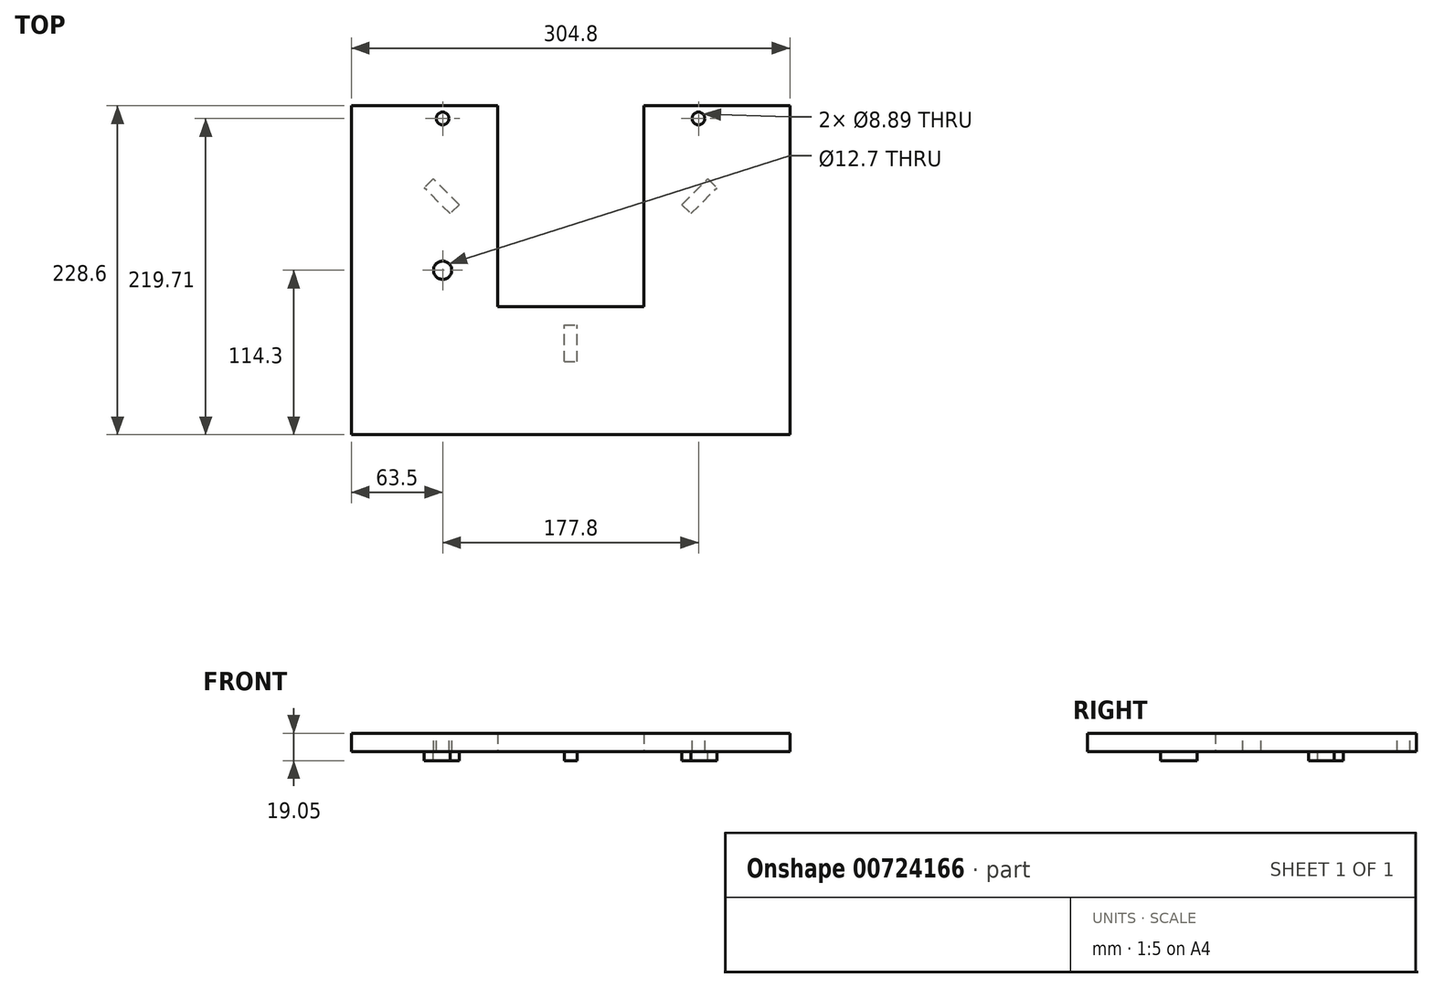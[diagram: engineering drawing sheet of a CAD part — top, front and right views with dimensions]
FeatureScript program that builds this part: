
annotation { "Feature Type Name" : "Feature", "Feature Type Description" : "" }
export const myFeature = defineFeature(function(context is Context, id is Id, definition is map)
    precondition{}
    {
        {
            var Q0;
            Q0=qCreatedBy(makeId("Top.planeOp"),FACE);
            var sketch = newSketch(context, id + "F0", { "sketchPlane" : qUnion([Q0])});
            skLineSegment(sketch, "E0.bottom", {"start": v(152.4, 114.3) * mm, "end": v(-152.4, 114.3) * mm});
            skLineSegment(sketch, "E0.top", {"start": v(152.4, -114.3) * mm, "end": v(-152.4, -114.3) * mm});
            skLineSegment(sketch, "E0.left", {"start": v(152.4, 114.3) * mm, "end": v(152.4, -114.3) * mm});
            skLineSegment(sketch, "E0.right", {"start": v(-152.4, 114.3) * mm, "end": v(-152.4, -114.3) * mm});
            skPoint(sketch, "E0.middle", {"position": v(0, 0) * mm});
            skLineSegment(sketch, "E1.bottom", {"start": v(-50.8, 114.3) * mm, "end": v(50.8, 114.3) * mm});
            skLineSegment(sketch, "E1.top", {"start": v(-50.8, -25.4) * mm, "end": v(50.8, -25.4) * mm});
            skLineSegment(sketch, "E1.left", {"start": v(-50.8, 114.3) * mm, "end": v(-50.8, -25.4) * mm});
            skLineSegment(sketch, "E1.right", {"start": v(50.8, 114.3) * mm, "end": v(50.8, -25.4) * mm});
            skLineSegment(sketch, "E2", {"start": v(50.8, 67.36) * mm, "end": v(152.4, 67.36) * mm, "construction": true});
            skSolve(sketch);
        }
        {
            var Q0;
            Q0=makeQuery(id+"F0.imprint","IMPRINT",FACE,{"disambiguationData":[TD([[makeQuery(id+"F0.imprint","IMPRINT",EDGE,{"derivedFrom":sQuery(id+"F0.wireOp",EDGE,"E0.bottom")}),1.0]])]});
            extrude(context, id + "F1", {"entities" : qUnion([Q0]), "depth" : 12.7 * mm, "offsetDistance" : 25.4 * mm});
        }
        {
            var Q0;
            Q0=makeQuery(id+"F1.opExtrude","CAP_FACE",FACE,{"disambiguationData":[OSD([sQuery(id+"F0.wireOp",EDGE,"E0.bottom"),sQuery(id+"F0.wireOp",EDGE,"E0.top"),sQuery(id+"F0.wireOp",EDGE,"E0.left"),sQuery(id+"F0.wireOp",EDGE,"E0.right"),sQuery(id+"F0.wireOp",EDGE,"E1.top"),sQuery(id+"F0.wireOp",EDGE,"E1.left"),sQuery(id+"F0.wireOp",EDGE,"E1.right")])],"isStart":false});
            var sketch = newSketch(context, id + "F2", { "sketchPlane" : qUnion([Q0])});
            skLineSegment(sketch, "E3", {"start": v(0, 0) * mm, "end": v(0, 105.41) * mm, "construction": true});
            skLineSegment(sketch, "E4", {"start": v(0, 105.41) * mm, "end": v(-88.9, 105.41) * mm, "construction": true});
            skLineSegment(sketch, "E5", {"start": v(0, 105.41) * mm, "end": v(88.9, 105.41) * mm, "construction": true});
            skCircle(sketch, "E6", {"center": v(-88.9, 105.41) * mm, "radius": 4.45 * mm});
            skCircle(sketch, "E7", {"center": v(88.9, 105.41) * mm, "radius": 4.45 * mm});
            skSolve(sketch);
        }
        {
            var Q0;
            Q0=makeQuery(id+"F1.opExtrude","CAP_FACE",FACE,{"disambiguationData":[OSD([sQuery(id+"F0.wireOp",EDGE,"E0.bottom"),sQuery(id+"F0.wireOp",EDGE,"E0.top"),sQuery(id+"F0.wireOp",EDGE,"E0.left"),sQuery(id+"F0.wireOp",EDGE,"E0.right"),sQuery(id+"F0.wireOp",EDGE,"E1.top"),sQuery(id+"F0.wireOp",EDGE,"E1.left"),sQuery(id+"F0.wireOp",EDGE,"E1.right")])],"isStart":false});
            var sketch = newSketch(context, id + "F3", { "sketchPlane" : qUnion([Q0])});
            skLineSegment(sketch, "E8", {"start": v(0, 0) * mm, "end": v(-88.9, 0) * mm, "construction": true});
            skCircle(sketch, "E9", {"center": v(-88.9, 0) * mm, "radius": 6.35 * mm});
            skSolve(sketch);
        }
        {
            var Q0;
            Q0 = qSketchRegion(id + "F3", true);
            extrude(context, id + "F4", {"entities" : qUnion([Q0]), "operationType" : NewBodyOperationType.REMOVE, "oppositeDirection" : true, "depth" : 25.4 * mm, "offsetDistance" : 25.4 * mm});
        }
        {
            var Q0;
            Q0 = qSketchRegion(id + "F2", true);
            extrude(context, id + "F5", {"entities" : qUnion([Q0]), "operationType" : NewBodyOperationType.REMOVE, "oppositeDirection" : true, "depth" : 25.4 * mm, "offsetDistance" : 25.4 * mm});
        }
        {
            var Q0;
            Q0=makeQuery(id+"F1.opExtrude","CAP_FACE",FACE,{"disambiguationData":[OSD([sQuery(id+"F0.wireOp",EDGE,"E0.bottom"),sQuery(id+"F0.wireOp",EDGE,"E0.top"),sQuery(id+"F0.wireOp",EDGE,"E0.left"),sQuery(id+"F0.wireOp",EDGE,"E0.right"),sQuery(id+"F0.wireOp",EDGE,"E1.top"),sQuery(id+"F0.wireOp",EDGE,"E1.left"),sQuery(id+"F0.wireOp",EDGE,"E1.right")])],"isStart":true});
            var sketch = newSketch(context, id + "F6", { "sketchPlane" : qUnion([Q0])});
            skLineSegment(sketch, "E10", {"start": v(0, 0) * mm, "end": v(0, 143.7) * mm, "construction": true});
            skPoint(sketch, "E11.middle", {"position": v(0, 0) * mm});
            skLineSegment(sketch, "E12.bottom", {"start": v(77.41, -45.6) * mm, "end": v(83.7, -39.31) * mm});
            skLineSegment(sketch, "E12.top", {"start": v(95.38, -63.56) * mm, "end": v(101.66, -57.28) * mm});
            skLineSegment(sketch, "E12.left", {"start": v(77.41, -45.6) * mm, "end": v(95.38, -63.56) * mm});
            skLineSegment(sketch, "E12.right", {"start": v(83.7, -39.31) * mm, "end": v(101.66, -57.28) * mm});
            skLineSegment(sketch, "E13.bottom", {"start": v(-4.45, 63.5) * mm, "end": v(4.44, 63.5) * mm});
            skLineSegment(sketch, "E13.top", {"start": v(-4.45, 38.1) * mm, "end": v(4.44, 38.1) * mm});
            skLineSegment(sketch, "E13.left", {"start": v(-4.45, 63.5) * mm, "end": v(-4.45, 38.1) * mm});
            skLineSegment(sketch, "E13.right", {"start": v(4.45, 63.5) * mm, "end": v(4.45, 38.1) * mm});
            skPoint(sketch, "E13.middle", {"position": v(0, 50.8) * mm});
            skLineSegment(sketch, "E14.bottom", {"start": v(-77.41, -45.6) * mm, "end": v(-83.7, -39.31) * mm});
            skLineSegment(sketch, "E14.top", {"start": v(-95.38, -63.56) * mm, "end": v(-101.66, -57.28) * mm});
            skLineSegment(sketch, "E14.left", {"start": v(-77.41, -45.6) * mm, "end": v(-95.38, -63.56) * mm});
            skLineSegment(sketch, "E14.right", {"start": v(-83.7, -39.31) * mm, "end": v(-101.66, -57.28) * mm});
            skLineSegment(sketch, "E15", {"start": v(152.4, -114.3) * mm, "end": v(70.08, -31.98) * mm, "construction": true});
            skLineSegment(sketch, "E16", {"start": v(-152.4, -114.3) * mm, "end": v(-69.25, -31.15) * mm, "construction": true});
            skSolve(sketch);
        }
        {
            var Q0;
            Q0 = qSketchRegion(id + "F6", true);
            extrude(context, id + "F7", {"entities" : qUnion([Q0]), "operationType" : NewBodyOperationType.ADD, "depth" : 6.35 * mm, "offsetDistance" : 25.4 * mm});
        }
    });
